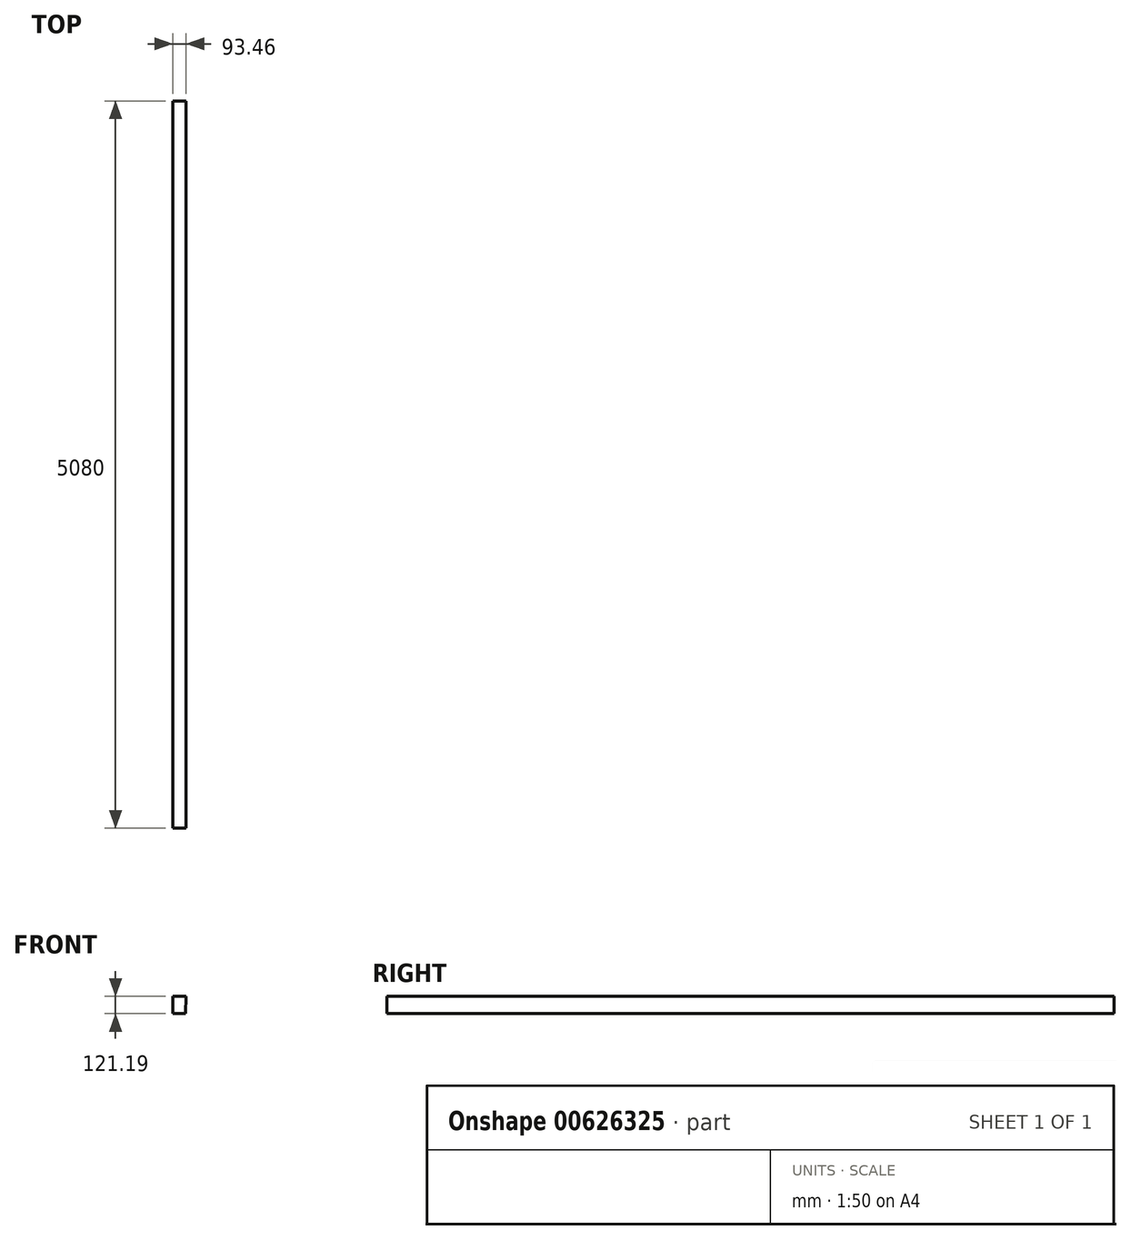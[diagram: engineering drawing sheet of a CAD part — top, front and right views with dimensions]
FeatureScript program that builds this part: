
annotation { "Feature Type Name" : "Feature", "Feature Type Description" : "" }
export const myFeature = defineFeature(function(context is Context, id is Id, definition is map)
    precondition{}
    {
        {
            var Q0;
            Q0=qCreatedBy(makeId("Front.planeOp"),FACE);
            var sketch = newSketch(context, id + "F0", { "sketchPlane" : qUnion([Q0])});
            skLineSegment(sketch, "E0", {"start": v(0, 0) * mm, "end": v(0, 121.2) * mm});
            skLineSegment(sketch, "E1", {"start": v(0, 121.2) * mm, "end": v(93.46, 121.2) * mm});
            skLineSegment(sketch, "E2", {"start": v(93.46, 121.2) * mm, "end": v(90.78, 0) * mm});
            skLineSegment(sketch, "E3", {"start": v(90.78, 0) * mm, "end": v(0, 0) * mm});
            skSolve(sketch);
        }
        {
            var Q0;
            Q0=makeQuery(id+"F0.imprint","IMPRINT",FACE,{"disambiguationData":[TD([[makeQuery(id+"F0.imprint","IMPRINT",EDGE,{"derivedFrom":sQuery(id+"F0.wireOp",EDGE,"E0")}),-1.0]])]});
            extrude(context, id + "F1", {"entities" : qUnion([Q0]), "oppositeDirection" : true, "depth" : 5080 * mm, "offsetDistance" : 25.4 * mm});
        }
    });
